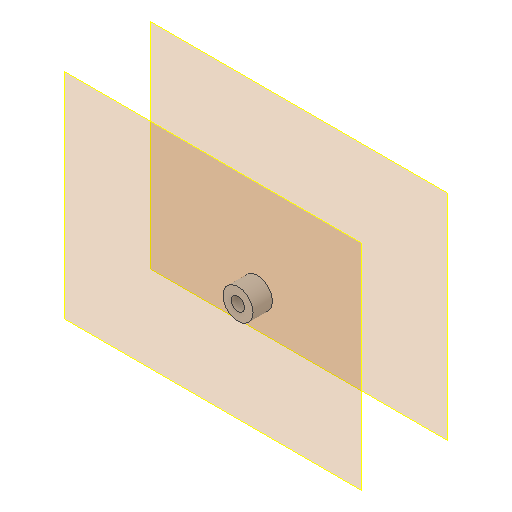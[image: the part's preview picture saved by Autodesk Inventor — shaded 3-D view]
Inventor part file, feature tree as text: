
AUTODESK INVENTOR PART (.ipt)
format: ipt  version: 2022 (Build 260153000, 153)  size: 91,648 bytes
history: native  units: mm
features: other x4, plane x2, extrude x1, sketch x1, reference x1
ambient origin geometry x8: Origin, YZ Plane, XZ Plane, XY Plane, X Axis, Y Axis, Z Axis, Center Point
bodies: Solid1 (feature_tree)
feature tree (9):
  plane  "Work Plane1"
  plane  "Work Plane2"
  extrude  "Extrusion1"  Depth=7.0mm TaperAngle=0.0deg
  sketch  "Sketch1"  dims[d0=3.0mm d1=7.0mm d2=0.0mm]
  reference  "Reference1"
  other  "Assembly_neje_slide_y_wellplateholder_20mmrod.iam"
  other  "Assembly_neje_slide_y_20mmrod:1"
  other  "Neje_slide_y_20mmrod_lowerplate:1"
  other  "Neje_slide_y_20mmrod_upperplate:1"
